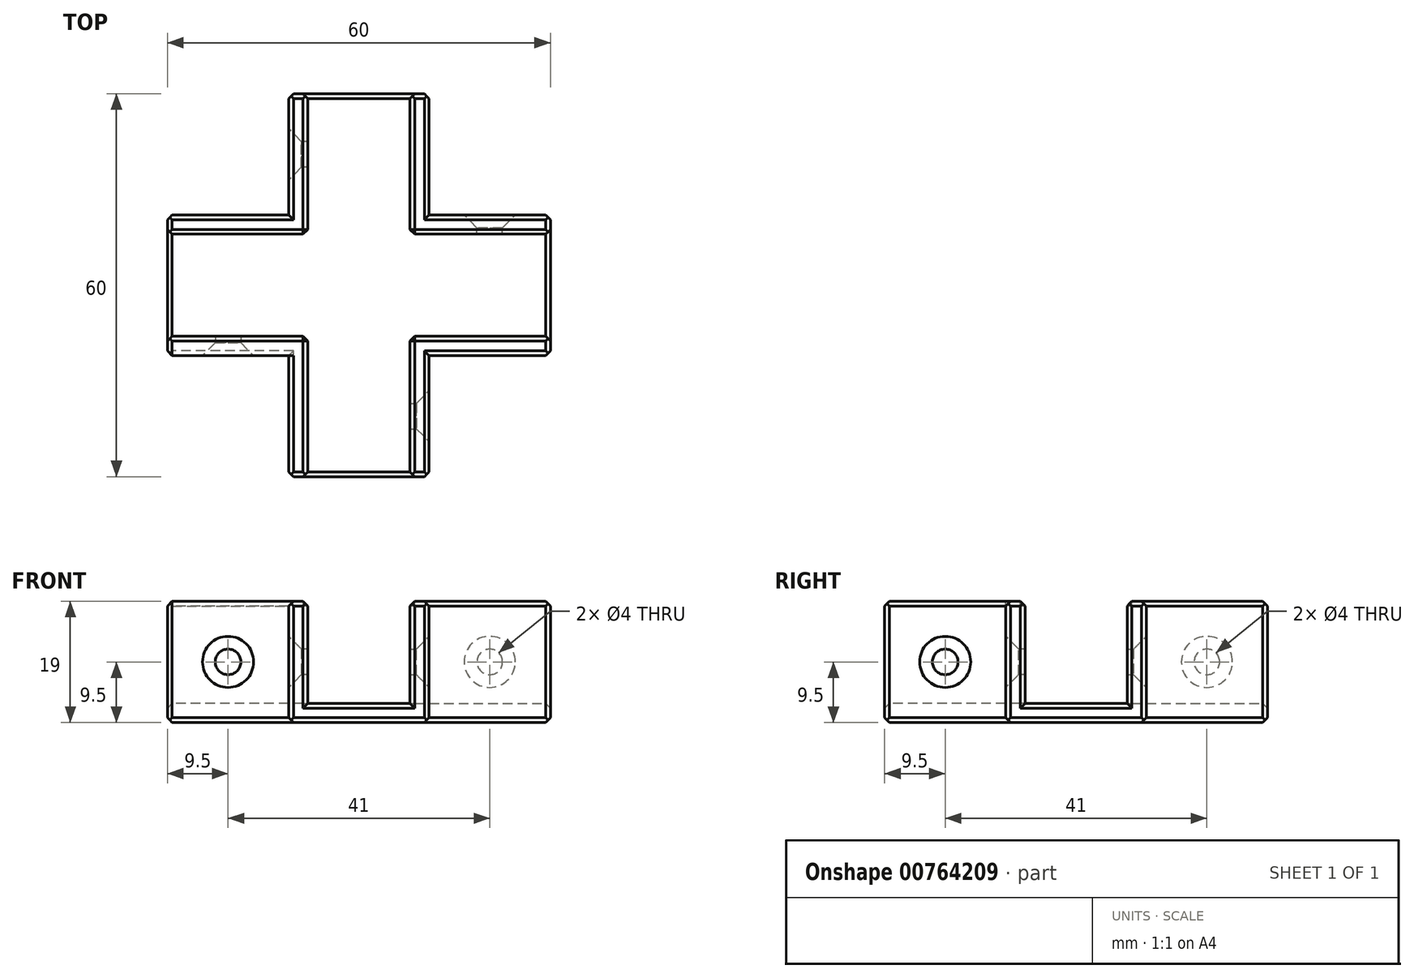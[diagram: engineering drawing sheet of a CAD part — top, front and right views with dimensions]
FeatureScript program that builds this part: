
annotation { "Feature Type Name" : "Feature", "Feature Type Description" : "" }
export const myFeature = defineFeature(function(context is Context, id is Id, definition is map)
    precondition{}
    {
        {
            var Q0;
            Q0=qCreatedBy(makeId("Top.planeOp"),FACE);
            var sketch = newSketch(context, id + "F0", { "sketchPlane" : qUnion([Q0])});
            skLineSegment(sketch, "E0.bottom", {"start": v(0, 0) * mm, "end": v(60, 0) * mm});
            skLineSegment(sketch, "E0.top", {"start": v(0, 22) * mm, "end": v(60, 22) * mm});
            skLineSegment(sketch, "E0.left", {"start": v(0, 0) * mm, "end": v(0, 22) * mm});
            skLineSegment(sketch, "E0.right", {"start": v(60, 0) * mm, "end": v(60, 22) * mm});
            skLineSegment(sketch, "E1", {"start": v(0, 22) * mm, "end": v(19, 22) * mm});
            skLineSegment(sketch, "E2.bottom", {"start": v(19, 22) * mm, "end": v(41, 22) * mm});
            skLineSegment(sketch, "E2.top", {"start": v(19, 41) * mm, "end": v(41, 41) * mm});
            skLineSegment(sketch, "E2.left", {"start": v(19, 22) * mm, "end": v(19, 41) * mm});
            skLineSegment(sketch, "E2.right", {"start": v(41, 22) * mm, "end": v(41, 41) * mm});
            skLineSegment(sketch, "E3", {"start": v(0, 0) * mm, "end": v(19, 0) * mm});
            skLineSegment(sketch, "E4.bottom", {"start": v(19, 0) * mm, "end": v(41, 0) * mm});
            skLineSegment(sketch, "E4.top", {"start": v(19, -19) * mm, "end": v(41, -19) * mm});
            skLineSegment(sketch, "E4.left", {"start": v(19, 0) * mm, "end": v(19, -19) * mm});
            skLineSegment(sketch, "E4.right", {"start": v(41, 0) * mm, "end": v(41, -19) * mm});
            skSolve(sketch);
        }
        {
            var Q0;
            {var subQ12=sQuery(id+"F0.wireOp",EDGE,"E0.left");Q0=qUnion([makeQuery(id+"F0.imprint","IMPRINT",FACE,{"disambiguationData":[TD([[makeQuery(id+"F0.imprint","IMPRINT",EDGE,{"derivedFrom":sQuery(id+"F0.wireOp",EDGE,"E4.top")}),1.0]])]}),makeQuery(id+"F0.imprint","IMPRINT",FACE,{"disambiguationData":[TD([[makeQuery(id+"F0.imprint","IMPRINT",EDGE,{"derivedFrom":sQuery(id+"F0.wireOp",EDGE,"E2.top")}),-1.0]])]}),makeQuery(id+"F0.imprint","IMPRINT",FACE,{"disambiguationData":[TD([[makeQuery(id+"F0.imprint","IMPRINT",EDGE,{"derivedFrom":subQ12}),-1.0]])]})]);}
            extrude(context, id + "F1", {"entities" : qUnion([Q0]), "depth" : 3 * mm, "offsetDistance" : 25 * mm});
        }
        {
            var Q0;
            Q0=makeQuery(id+"F1.opExtrude","CAP_FACE",FACE,{"disambiguationData":[OSD([sQuery(id+"F0.wireOp",EDGE,"E0.bottom"),sQuery(id+"F0.wireOp",EDGE,"E0.top"),sQuery(id+"F0.wireOp",EDGE,"E0.left"),sQuery(id+"F0.wireOp",EDGE,"E0.right"),sQuery(id+"F0.wireOp",EDGE,"E2.top"),sQuery(id+"F0.wireOp",EDGE,"E2.left"),sQuery(id+"F0.wireOp",EDGE,"E2.right"),sQuery(id+"F0.wireOp",EDGE,"E4.top"),sQuery(id+"F0.wireOp",EDGE,"E4.left"),sQuery(id+"F0.wireOp",EDGE,"E4.right")])],"isStart":false});
            var sketch = newSketch(context, id + "F2", { "sketchPlane" : qUnion([Q0])});
            skLineSegment(sketch, "E5.bottom", {"start": v(0, 22) * mm, "end": v(19, 22) * mm});
            skLineSegment(sketch, "E5.top", {"start": v(0, 19) * mm, "end": v(19, 19) * mm});
            skLineSegment(sketch, "E5.left", {"start": v(0, 22) * mm, "end": v(0, 19) * mm});
            skLineSegment(sketch, "E5.right", {"start": v(19, 22) * mm, "end": v(19, 19) * mm});
            skLineSegment(sketch, "E6.bottom", {"start": v(19, 0) * mm, "end": v(0, 0) * mm});
            skLineSegment(sketch, "E6.top", {"start": v(19, 3) * mm, "end": v(0, 3) * mm});
            skLineSegment(sketch, "E6.left", {"start": v(19, 0) * mm, "end": v(19, 3) * mm});
            skLineSegment(sketch, "E6.right", {"start": v(0, 0) * mm, "end": v(0, 3) * mm});
            skLineSegment(sketch, "E7.bottom", {"start": v(19, 19) * mm, "end": v(22, 19) * mm});
            skLineSegment(sketch, "E7.top", {"start": v(19, 41) * mm, "end": v(22, 41) * mm});
            skLineSegment(sketch, "E7.left", {"start": v(19, 19) * mm, "end": v(19, 41) * mm});
            skLineSegment(sketch, "E7.right", {"start": v(22, 19) * mm, "end": v(22, 41) * mm});
            skLineSegment(sketch, "E8.bottom", {"start": v(19, 3) * mm, "end": v(22, 3) * mm});
            skLineSegment(sketch, "E8.top", {"start": v(19, -19) * mm, "end": v(22, -19) * mm});
            skLineSegment(sketch, "E8.left", {"start": v(19, 3) * mm, "end": v(19, -19) * mm});
            skLineSegment(sketch, "E8.right", {"start": v(22, 3) * mm, "end": v(22, -19) * mm});
            skLineSegment(sketch, "E9.bottom", {"start": v(41, 22) * mm, "end": v(38, 22) * mm});
            skLineSegment(sketch, "E9.top", {"start": v(41, 41) * mm, "end": v(38, 41) * mm});
            skLineSegment(sketch, "E9.left", {"start": v(41, 22) * mm, "end": v(41, 41) * mm});
            skLineSegment(sketch, "E9.right", {"start": v(38, 22) * mm, "end": v(38, 41) * mm});
            skLineSegment(sketch, "E10.bottom", {"start": v(41, 0) * mm, "end": v(38, 0) * mm});
            skLineSegment(sketch, "E10.top", {"start": v(41, -19) * mm, "end": v(38, -19) * mm});
            skLineSegment(sketch, "E10.left", {"start": v(41, 0) * mm, "end": v(41, -19) * mm});
            skLineSegment(sketch, "E10.right", {"start": v(38, 0) * mm, "end": v(38, -19) * mm});
            skLineSegment(sketch, "E11.bottom", {"start": v(38, 22) * mm, "end": v(60, 22) * mm});
            skLineSegment(sketch, "E11.top", {"start": v(38, 19) * mm, "end": v(60, 19) * mm});
            skLineSegment(sketch, "E11.left", {"start": v(38, 22) * mm, "end": v(38, 19) * mm});
            skLineSegment(sketch, "E11.right", {"start": v(60, 22) * mm, "end": v(60, 19) * mm});
            skLineSegment(sketch, "E12.bottom", {"start": v(38, 0) * mm, "end": v(60, 0) * mm});
            skLineSegment(sketch, "E12.top", {"start": v(38, 3) * mm, "end": v(60, 3) * mm});
            skLineSegment(sketch, "E12.left", {"start": v(38, 0) * mm, "end": v(38, 3) * mm});
            skLineSegment(sketch, "E12.right", {"start": v(60, 0) * mm, "end": v(60, 3) * mm});
            skSolve(sketch);
        }
        {
            var Q0;
            Q0 = qSketchRegion(id + "F2", true);
            extrude(context, id + "F3", {"entities" : qUnion([Q0]), "operationType" : NewBodyOperationType.ADD, "depth" : 16 * mm, "offsetDistance" : 25 * mm});
        }
        {
            var Q0;
            {var subQ0=sQuery(id+"F0.wireOp",EDGE,"E0.bottom");Q0=makeQuery(id+"F3.boolean.opBoolean","MERGE",FACE,{"derivedFrom":[makeQuery(id+"F1.opExtrude","SWEPT_FACE",FACE,{"disambiguationData":[OSD([subQ0]),TDD([makeQuery(id+"F0.imprint","IMPRINT",EDGE,{"disambiguationData":[TD([[makeQuery(id+"F0.imprint","INTERSECT",VERTEX,{"derivedFrom":[subQ0,sQuery(id+"F0.wireOp",EDGE,"E4.left")]}),1.0]])],"derivedFrom":subQ0})])]}),makeQuery(id+"F3.opExtrude","SWEPT_FACE",FACE,{"disambiguationData":[OSD([sQuery(id+"F2.wireOp",EDGE,"E6.bottom")])]})]});}
            var sketch = newSketch(context, id + "F4", { "sketchPlane" : qUnion([Q0])});
            skLineSegment(sketch, "E13", {"start": v(0, 19) * mm, "end": v(19, 0) * mm});
            skLineSegment(sketch, "E14", {"start": v(19, 0) * mm, "end": v(19, 19) * mm});
            skLineSegment(sketch, "E15", {"start": v(19, 19) * mm, "end": v(0, 0) * mm});
            skPoint(sketch, "E16", {"position": v(9.5, 9.5) * mm});
            skSolve(sketch);
        }
        {
            var Q0;
            Q0=sQuery(id+"F4.wireOp",VERTEX,"E16");
            var Q1;
            Q1=makeQuery(id+"F1.opExtrude","SWEPT_BODY",BODY,{"disambiguationData":[OSD([sQuery(id+"F0.wireOp",EDGE,"E0.bottom"),sQuery(id+"F0.wireOp",EDGE,"E0.top"),sQuery(id+"F0.wireOp",EDGE,"E0.left"),sQuery(id+"F0.wireOp",EDGE,"E0.right"),sQuery(id+"F0.wireOp",EDGE,"E2.top"),sQuery(id+"F0.wireOp",EDGE,"E2.left"),sQuery(id+"F0.wireOp",EDGE,"E2.right"),sQuery(id+"F0.wireOp",EDGE,"E4.top"),sQuery(id+"F0.wireOp",EDGE,"E4.left"),sQuery(id+"F0.wireOp",EDGE,"E4.right")])]});
            hole(context, id + "F5", {"style" : HoleStyle.C_SINK, "endStyle" : HoleEndStyle.BLIND, "holeDiameter" : 4 * mm, "cSinkDiameter" : 8 * mm, "cSinkAngle" : 90 * degree, "majorDiameter" : 5 * mm, "holeDepth" : 12 * mm, "isTappedThrough" : true, "tappedDepth" : 12 * mm, "tapClearance" : 3, "locations" : qUnion([Q0]), "scope" : qUnion([Q1])});
        }
        {
            var Q0;
            Q0=makeQuery(id+"F3.boolean.opBoolean","MERGE",FACE,{"derivedFrom":[makeQuery(id+"F1.opExtrude","SWEPT_FACE",FACE,{"disambiguationData":[OSD([sQuery(id+"F0.wireOp",EDGE,"E4.right")])]}),makeQuery(id+"F3.opExtrude","SWEPT_FACE",FACE,{"disambiguationData":[OSD([sQuery(id+"F2.wireOp",EDGE,"E10.left")])]})]});
            var sketch = newSketch(context, id + "F6", { "sketchPlane" : qUnion([Q0])});
            skLineSegment(sketch, "E17", {"start": v(-19, 19) * mm, "end": v(0, 0) * mm});
            skLineSegment(sketch, "E18", {"start": v(0, 0) * mm, "end": v(0, 19) * mm});
            skLineSegment(sketch, "E19", {"start": v(0, 19) * mm, "end": v(-19, 0) * mm});
            skPoint(sketch, "E20", {"position": v(-9.5, 9.5) * mm});
            skSolve(sketch);
        }
        {
            var Q0;
            Q0=sQuery(id+"F6.wireOp",VERTEX,"E20");
            var Q1;
            Q1=makeQuery(id+"F1.opExtrude","SWEPT_BODY",BODY,{"disambiguationData":[OSD([sQuery(id+"F0.wireOp",EDGE,"E0.bottom"),sQuery(id+"F0.wireOp",EDGE,"E0.top"),sQuery(id+"F0.wireOp",EDGE,"E0.left"),sQuery(id+"F0.wireOp",EDGE,"E0.right"),sQuery(id+"F0.wireOp",EDGE,"E2.top"),sQuery(id+"F0.wireOp",EDGE,"E2.left"),sQuery(id+"F0.wireOp",EDGE,"E2.right"),sQuery(id+"F0.wireOp",EDGE,"E4.top"),sQuery(id+"F0.wireOp",EDGE,"E4.left"),sQuery(id+"F0.wireOp",EDGE,"E4.right")])]});
            hole(context, id + "F7", {"style" : HoleStyle.C_SINK, "endStyle" : HoleEndStyle.BLIND, "holeDiameter" : 4 * mm, "cSinkDiameter" : 8 * mm, "cSinkAngle" : 90 * degree, "majorDiameter" : 5 * mm, "holeDepth" : 12 * mm, "isTappedThrough" : true, "tappedDepth" : 12 * mm, "tapClearance" : 3, "locations" : qUnion([Q0]), "scope" : qUnion([Q1])});
        }
        {
            var Q0;
            {var subQ0=sQuery(id+"F0.wireOp",EDGE,"E0.top");Q0=makeQuery(id+"F3.boolean.opBoolean","MERGE",FACE,{"derivedFrom":[makeQuery(id+"F1.opExtrude","SWEPT_FACE",FACE,{"disambiguationData":[OSD([subQ0]),TDD([makeQuery(id+"F0.imprint","IMPRINT",EDGE,{"disambiguationData":[TD([[makeQuery(id+"F0.imprint","INTERSECT",VERTEX,{"derivedFrom":[subQ0,sQuery(id+"F0.wireOp",EDGE,"E0.right")]}),1.0]])],"derivedFrom":subQ0})])]}),makeQuery(id+"F3.opExtrude","SWEPT_FACE",FACE,{"disambiguationData":[OSD([sQuery(id+"F2.wireOp",EDGE,"E11.bottom")])]})]});}
            var sketch = newSketch(context, id + "F8", { "sketchPlane" : qUnion([Q0])});
            skLineSegment(sketch, "E21", {"start": v(-41, 19) * mm, "end": v(-60, 0) * mm});
            skLineSegment(sketch, "E22", {"start": v(-60, 0) * mm, "end": v(-60, 19) * mm});
            skLineSegment(sketch, "E23", {"start": v(-60, 19) * mm, "end": v(-41, 0) * mm});
            skPoint(sketch, "E24", {"position": v(-50.5, 9.5) * mm});
            skSolve(sketch);
        }
        {
            var Q0;
            Q0=sQuery(id+"F8.wireOp",VERTEX,"E24");
            var Q1;
            Q1=makeQuery(id+"F1.opExtrude","SWEPT_BODY",BODY,{"disambiguationData":[OSD([sQuery(id+"F0.wireOp",EDGE,"E0.bottom"),sQuery(id+"F0.wireOp",EDGE,"E0.top"),sQuery(id+"F0.wireOp",EDGE,"E0.left"),sQuery(id+"F0.wireOp",EDGE,"E0.right"),sQuery(id+"F0.wireOp",EDGE,"E2.top"),sQuery(id+"F0.wireOp",EDGE,"E2.left"),sQuery(id+"F0.wireOp",EDGE,"E2.right"),sQuery(id+"F0.wireOp",EDGE,"E4.top"),sQuery(id+"F0.wireOp",EDGE,"E4.left"),sQuery(id+"F0.wireOp",EDGE,"E4.right")])]});
            hole(context, id + "F9", {"style" : HoleStyle.C_SINK, "endStyle" : HoleEndStyle.BLIND, "holeDiameter" : 4 * mm, "cSinkDiameter" : 8 * mm, "cSinkAngle" : 90 * degree, "majorDiameter" : 5 * mm, "holeDepth" : 12 * mm, "isTappedThrough" : true, "tappedDepth" : 12 * mm, "tapClearance" : 3, "locations" : qUnion([Q0]), "scope" : qUnion([Q1])});
        }
        {
            var Q0;
            Q0=makeQuery(id+"F3.boolean.opBoolean","MERGE",FACE,{"derivedFrom":[makeQuery(id+"F1.opExtrude","SWEPT_FACE",FACE,{"disambiguationData":[OSD([sQuery(id+"F0.wireOp",EDGE,"E2.left")])]}),makeQuery(id+"F3.opExtrude","SWEPT_FACE",FACE,{"disambiguationData":[OSD([sQuery(id+"F2.wireOp",EDGE,"E7.left")])]})]});
            var sketch = newSketch(context, id + "F10", { "sketchPlane" : qUnion([Q0])});
            skLineSegment(sketch, "E25", {"start": v(-41, 19) * mm, "end": v(-22, 0) * mm});
            skLineSegment(sketch, "E26", {"start": v(-22, 19) * mm, "end": v(-41, 0) * mm});
            skPoint(sketch, "E27", {"position": v(-31.5, 9.5) * mm});
            skSolve(sketch);
        }
        {
            var Q0;
            Q0=sQuery(id+"F10.wireOp",VERTEX,"E27");
            var Q1;
            Q1=makeQuery(id+"F1.opExtrude","SWEPT_BODY",BODY,{"disambiguationData":[OSD([sQuery(id+"F0.wireOp",EDGE,"E0.bottom"),sQuery(id+"F0.wireOp",EDGE,"E0.top"),sQuery(id+"F0.wireOp",EDGE,"E0.left"),sQuery(id+"F0.wireOp",EDGE,"E0.right"),sQuery(id+"F0.wireOp",EDGE,"E2.top"),sQuery(id+"F0.wireOp",EDGE,"E2.left"),sQuery(id+"F0.wireOp",EDGE,"E2.right"),sQuery(id+"F0.wireOp",EDGE,"E4.top"),sQuery(id+"F0.wireOp",EDGE,"E4.left"),sQuery(id+"F0.wireOp",EDGE,"E4.right")])]});
            hole(context, id + "F11", {"style" : HoleStyle.C_SINK, "endStyle" : HoleEndStyle.BLIND, "holeDiameter" : 4 * mm, "cSinkDiameter" : 8 * mm, "cSinkAngle" : 90 * degree, "majorDiameter" : 5 * mm, "holeDepth" : 12 * mm, "isTappedThrough" : true, "tappedDepth" : 12 * mm, "tapClearance" : 3, "locations" : qUnion([Q0]), "scope" : qUnion([Q1])});
        }
        {
            var Q0;
            Q0=makeQuery(id+"F3.boolean.opBoolean","MERGE",FACE,{"derivedFrom":[makeQuery(id+"F1.opExtrude","SWEPT_FACE",FACE,{"disambiguationData":[OSD([sQuery(id+"F0.wireOp",EDGE,"E4.top")])]}),makeQuery(id+"F3.opExtrude","SWEPT_FACE",FACE,{"disambiguationData":[OSD([sQuery(id+"F2.wireOp",EDGE,"E8.top")])]}),makeQuery(id+"F3.opExtrude","SWEPT_FACE",FACE,{"disambiguationData":[OSD([sQuery(id+"F2.wireOp",EDGE,"E10.top")])]})]});
            var Q1;
            Q1=makeQuery(id+"F3.boolean.opBoolean","MERGE",FACE,{"derivedFrom":[makeQuery(id+"F1.opExtrude","SWEPT_FACE",FACE,{"disambiguationData":[OSD([sQuery(id+"F0.wireOp",EDGE,"E0.right")])]}),makeQuery(id+"F3.opExtrude","SWEPT_FACE",FACE,{"disambiguationData":[OSD([sQuery(id+"F2.wireOp",EDGE,"E11.right")])]}),makeQuery(id+"F3.opExtrude","SWEPT_FACE",FACE,{"disambiguationData":[OSD([sQuery(id+"F2.wireOp",EDGE,"E12.right")])]})]});
            var Q2;
            Q2=makeQuery(id+"F3.boolean.opBoolean","MERGE",FACE,{"derivedFrom":[makeQuery(id+"F1.opExtrude","SWEPT_FACE",FACE,{"disambiguationData":[OSD([sQuery(id+"F0.wireOp",EDGE,"E2.top")])]}),makeQuery(id+"F3.opExtrude","SWEPT_FACE",FACE,{"disambiguationData":[OSD([sQuery(id+"F2.wireOp",EDGE,"E7.top")])]}),makeQuery(id+"F3.opExtrude","SWEPT_FACE",FACE,{"disambiguationData":[OSD([sQuery(id+"F2.wireOp",EDGE,"E9.top")])]})]});
            var Q3;
            Q3=makeQuery(id+"F3.boolean.opBoolean","MERGE",FACE,{"derivedFrom":[makeQuery(id+"F1.opExtrude","SWEPT_FACE",FACE,{"disambiguationData":[OSD([sQuery(id+"F0.wireOp",EDGE,"E0.left")])]}),makeQuery(id+"F3.opExtrude","SWEPT_FACE",FACE,{"disambiguationData":[OSD([sQuery(id+"F2.wireOp",EDGE,"E5.left")])]}),makeQuery(id+"F3.opExtrude","SWEPT_FACE",FACE,{"disambiguationData":[OSD([sQuery(id+"F2.wireOp",EDGE,"E6.right")])]})]});
            chamfer(context, id + "F12", {"entities" : qUnion([Q0, Q1, Q2, Q3]), "width" : 0.75 * mm, "tangentPropagation" : true});
        }
        {
            var Q0;
            {var subQ0=sQuery(id+"F0.wireOp",EDGE,"E0.top");Q0=makeQuery(id+"F1.opExtrude","CAP_EDGE",EDGE,{"disambiguationData":[OSD([subQ0]),TDD([makeQuery(id+"F0.imprint","IMPRINT",EDGE,{"disambiguationData":[TD([[makeQuery(id+"F0.imprint","INTERSECT",VERTEX,{"derivedFrom":[subQ0,sQuery(id+"F0.wireOp",EDGE,"E2.left")]}),1.0]])],"derivedFrom":subQ0})])],"isStart":true});}
            var Q1;
            Q1=makeQuery(id+"F1.opExtrude","CAP_EDGE",EDGE,{"disambiguationData":[OSD([sQuery(id+"F0.wireOp",EDGE,"E2.left")])],"isStart":true});
            var Q2;
            Q2=makeQuery(id+"F1.opExtrude","CAP_EDGE",EDGE,{"disambiguationData":[OSD([sQuery(id+"F0.wireOp",EDGE,"E2.right")])],"isStart":true});
            var Q3;
            {var subQ0=sQuery(id+"F0.wireOp",EDGE,"E0.top");Q3=makeQuery(id+"F1.opExtrude","CAP_EDGE",EDGE,{"disambiguationData":[OSD([subQ0]),TDD([makeQuery(id+"F0.imprint","IMPRINT",EDGE,{"disambiguationData":[TD([[makeQuery(id+"F0.imprint","INTERSECT",VERTEX,{"derivedFrom":[subQ0,sQuery(id+"F0.wireOp",EDGE,"E0.right")]}),1.0]])],"derivedFrom":subQ0})])],"isStart":true});}
            var Q4;
            {var subQ0=sQuery(id+"F0.wireOp",EDGE,"E0.bottom");Q4=makeQuery(id+"F1.opExtrude","CAP_EDGE",EDGE,{"disambiguationData":[OSD([subQ0]),TDD([makeQuery(id+"F0.imprint","IMPRINT",EDGE,{"disambiguationData":[TD([[makeQuery(id+"F0.imprint","INTERSECT",VERTEX,{"derivedFrom":[subQ0,sQuery(id+"F0.wireOp",EDGE,"E0.right")]}),1.0]])],"derivedFrom":subQ0})])],"isStart":true});}
            var Q5;
            Q5=makeQuery(id+"F1.opExtrude","CAP_EDGE",EDGE,{"disambiguationData":[OSD([sQuery(id+"F0.wireOp",EDGE,"E4.right")])],"isStart":true});
            var Q6;
            Q6=makeQuery(id+"F1.opExtrude","CAP_EDGE",EDGE,{"disambiguationData":[OSD([sQuery(id+"F0.wireOp",EDGE,"E4.left")])],"isStart":true});
            var Q7;
            {var subQ0=sQuery(id+"F0.wireOp",EDGE,"E0.bottom");Q7=makeQuery(id+"F1.opExtrude","CAP_EDGE",EDGE,{"disambiguationData":[OSD([subQ0]),TDD([makeQuery(id+"F0.imprint","IMPRINT",EDGE,{"disambiguationData":[TD([[makeQuery(id+"F0.imprint","INTERSECT",VERTEX,{"derivedFrom":[subQ0,sQuery(id+"F0.wireOp",EDGE,"E4.left")]}),1.0]])],"derivedFrom":subQ0})])],"isStart":true});}
            chamfer(context, id + "F13", {"entities" : qUnion([Q0, Q1, Q2, Q3, Q4, Q5, Q6, Q7]), "width" : 0.75 * mm, "tangentPropagation" : true});
        }
        {
            var Q0;
            Q0=makeQuery(id+"F3.opExtrude","CAP_EDGE",EDGE,{"disambiguationData":[OSD([sQuery(id+"F2.wireOp",EDGE,"E12.bottom")])],"isStart":false});
            var Q1;
            Q1=makeQuery(id+"F3.opExtrude","CAP_EDGE",EDGE,{"disambiguationData":[OSD([sQuery(id+"F2.wireOp",EDGE,"E10.left")])],"isStart":false});
            var Q2;
            Q2=makeQuery(id+"F3.opExtrude","CAP_EDGE",EDGE,{"disambiguationData":[OSD([sQuery(id+"F2.wireOp",EDGE,"E10.right"),sQuery(id+"F2.wireOp",EDGE,"E12.left")])],"isStart":false});
            var Q3;
            Q3=makeQuery(id+"F3.opExtrude","CAP_EDGE",EDGE,{"disambiguationData":[OSD([sQuery(id+"F2.wireOp",EDGE,"E12.top")])],"isStart":false});
            var Q4;
            Q4=makeQuery(id+"F3.opExtrude","SWEPT_EDGE",EDGE,{"disambiguationData":[OSD([sQuery(id+"F2.wireOp",EDGE,"E12.top"),sQuery(id+"F2.wireOp",EDGE,"E12.left")])]});
            var Q5;
            Q5=makeQuery(id+"F3.opExtrude","CAP_EDGE",EDGE,{"disambiguationData":[OSD([sQuery(id+"F2.wireOp",EDGE,"E8.right")])],"isStart":false});
            var Q6;
            Q6=makeQuery(id+"F3.opExtrude","CAP_EDGE",EDGE,{"disambiguationData":[OSD([sQuery(id+"F2.wireOp",EDGE,"E8.left")])],"isStart":false});
            var Q7;
            Q7=makeQuery(id+"F3.opExtrude","CAP_EDGE",EDGE,{"disambiguationData":[OSD([sQuery(id+"F2.wireOp",EDGE,"E6.top"),sQuery(id+"F2.wireOp",EDGE,"E8.bottom")])],"isStart":false});
            var Q8;
            Q8=makeQuery(id+"F3.opExtrude","SWEPT_EDGE",EDGE,{"disambiguationData":[OSD([sQuery(id+"F2.wireOp",EDGE,"E8.bottom"),sQuery(id+"F2.wireOp",EDGE,"E8.right")])]});
            var Q9;
            Q9=makeQuery(id+"F3.opExtrude","CAP_EDGE",EDGE,{"disambiguationData":[OSD([sQuery(id+"F2.wireOp",EDGE,"E5.top"),sQuery(id+"F2.wireOp",EDGE,"E7.bottom")])],"isStart":false});
            var Q10;
            Q10=makeQuery(id+"F3.opExtrude","CAP_EDGE",EDGE,{"disambiguationData":[OSD([sQuery(id+"F2.wireOp",EDGE,"E5.bottom")])],"isStart":false});
            var Q11;
            Q11=makeQuery(id+"F3.opExtrude","CAP_EDGE",EDGE,{"disambiguationData":[OSD([sQuery(id+"F2.wireOp",EDGE,"E7.left")])],"isStart":false});
            var Q12;
            Q12=makeQuery(id+"F3.opExtrude","CAP_EDGE",EDGE,{"disambiguationData":[OSD([sQuery(id+"F2.wireOp",EDGE,"E7.right")])],"isStart":false});
            var Q13;
            Q13=makeQuery(id+"F3.opExtrude","SWEPT_EDGE",EDGE,{"disambiguationData":[OSD([sQuery(id+"F2.wireOp",EDGE,"E7.bottom"),sQuery(id+"F2.wireOp",EDGE,"E7.right")])]});
            var Q14;
            Q14=makeQuery(id+"F3.opExtrude","CAP_EDGE",EDGE,{"disambiguationData":[OSD([sQuery(id+"F2.wireOp",EDGE,"E11.top")])],"isStart":false});
            var Q15;
            Q15=makeQuery(id+"F3.opExtrude","CAP_EDGE",EDGE,{"disambiguationData":[OSD([sQuery(id+"F2.wireOp",EDGE,"E11.bottom")])],"isStart":false});
            var Q16;
            Q16=makeQuery(id+"F3.opExtrude","CAP_EDGE",EDGE,{"disambiguationData":[OSD([sQuery(id+"F2.wireOp",EDGE,"E9.left")])],"isStart":false});
            var Q17;
            Q17=makeQuery(id+"F3.opExtrude","CAP_EDGE",EDGE,{"disambiguationData":[OSD([sQuery(id+"F2.wireOp",EDGE,"E9.right"),sQuery(id+"F2.wireOp",EDGE,"E11.left")])],"isStart":false});
            var Q18;
            Q18=makeQuery(id+"F3.opExtrude","SWEPT_EDGE",EDGE,{"disambiguationData":[OSD([sQuery(id+"F2.wireOp",EDGE,"E11.top"),sQuery(id+"F2.wireOp",EDGE,"E11.left")])]});
            chamfer(context, id + "F14", {"entities" : qUnion([Q0, Q1, Q2, Q3, Q4, Q5, Q6, Q7, Q8, Q9, Q10, Q11, Q12, Q13, Q14, Q15, Q16, Q17, Q18]), "width" : 0.75 * mm, "tangentPropagation" : true});
        }
    });
